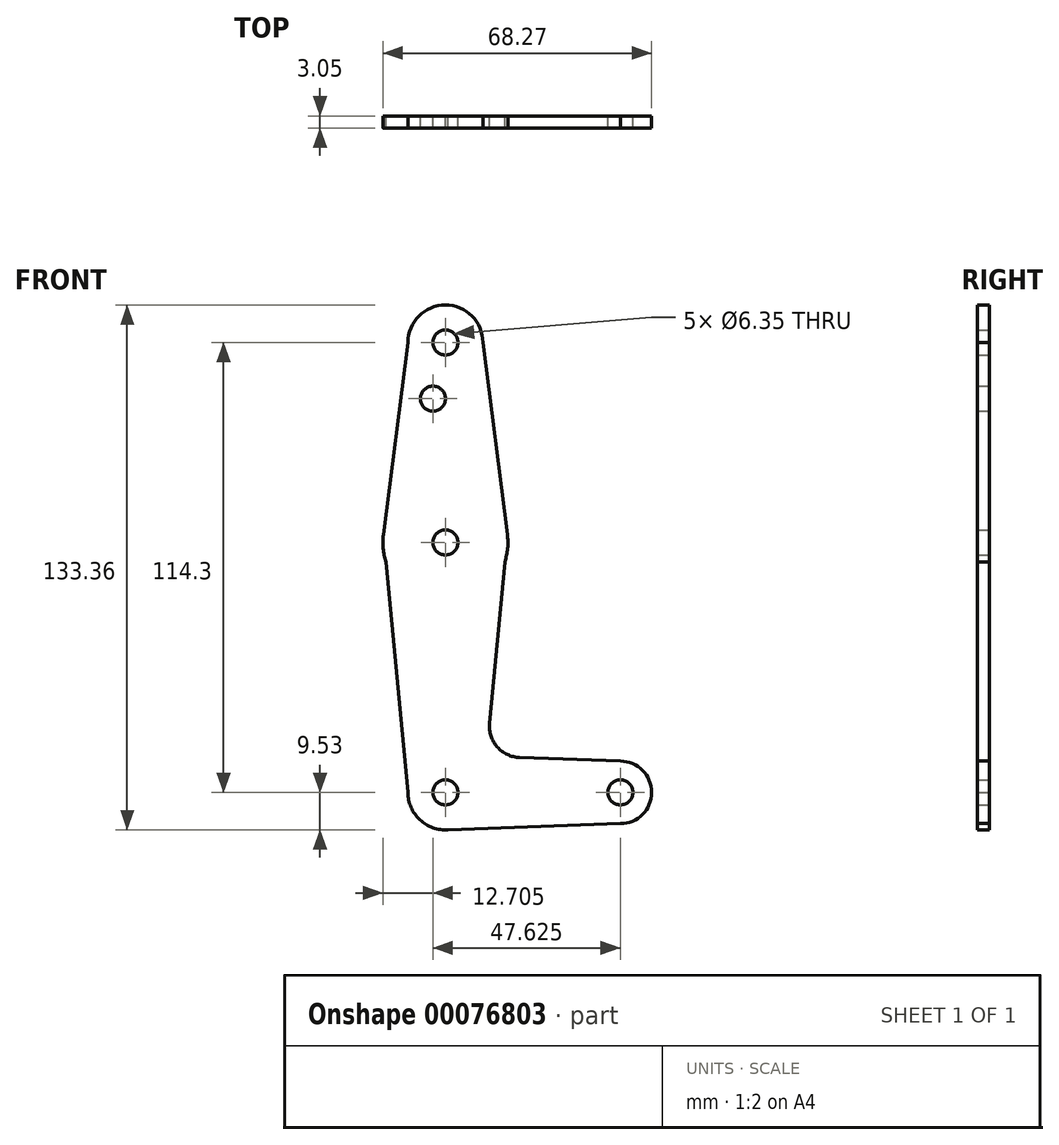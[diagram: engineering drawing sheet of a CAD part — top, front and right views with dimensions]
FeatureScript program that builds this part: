
annotation { "Feature Type Name" : "Feature", "Feature Type Description" : "" }
export const myFeature = defineFeature(function(context is Context, id is Id, definition is map)
    precondition{}
    {
        {
            var Q0;
            Q0=qCreatedBy(makeId("Front.planeOp"),FACE);
            var sketch = newSketch(context, id + "F0", { "sketchPlane" : qUnion([Q0])});
            skCircle(sketch, "E0", {"center": v(0, 114.3) * mm, "radius": 9.53 * mm});
            skLineSegment(sketch, "E1", {"start": v(0, 114.3) * mm, "end": v(0, 63.5) * mm, "construction": true});
            skCircle(sketch, "E2", {"center": v(0, 63.5) * mm, "radius": 15.88 * mm});
            skLineSegment(sketch, "E3", {"start": v(0, 63.5) * mm, "end": v(0, 0) * mm, "construction": true});
            skCircle(sketch, "E4", {"center": v(0, 0) * mm, "radius": 9.53 * mm});
            skLineSegment(sketch, "E5", {"start": v(0, 0) * mm, "end": v(44.45, 0) * mm, "construction": true});
            skCircle(sketch, "E6", {"center": v(44.45, 0) * mm, "radius": 7.94 * mm});
            skLineSegment(sketch, "E7", {"start": v(9.52, 114.3) * mm, "end": v(15.75, 65.5) * mm});
            skLineSegment(sketch, "E8", {"start": v(-9.53, 114.3) * mm, "end": v(-15.75, 65.5) * mm});
            skLineSegment(sketch, "E9", {"start": v(0, -9.53) * mm, "end": v(44.45, -7.94) * mm});
            skCircle(sketch, "E10", {"center": v(0, 114.3) * mm, "radius": 3.18 * mm});
            skCircle(sketch, "E11", {"center": v(0, 63.5) * mm, "radius": 3.18 * mm});
            skCircle(sketch, "E12", {"center": v(0, 0) * mm, "radius": 3.18 * mm});
            skCircle(sketch, "E13", {"center": v(44.45, 0) * mm, "radius": 3.18 * mm});
            skCircle(sketch, "E14", {"center": v(-3.18, 100.03) * mm, "radius": 3.18 * mm});
            skLineSegment(sketch, "E15", {"start": v(15.75, 65.5) * mm, "end": v(11.22, 17.55) * mm});
            skLineSegment(sketch, "E16", {"start": v(44.45, 7.94) * mm, "end": v(18.85, 8.86) * mm});
            skPoint(sketch, "E17.newPointA", {"position": v(9.57, 0) * mm});
            skPoint(sketch, "E17.newPointB", {"position": v(0, 9.53) * mm});
            skArc(sketch, "E17.filletArc", {"start": v(11.22, 17.55) * mm, "mid": v(13.16, 11.56) * mm, "end": v(18.85, 8.86) * mm});
            skLineSegment(sketch, "E18", {"start": v(-9.53, 0) * mm, "end": v(-15.75, 65.5) * mm});
            skSolve(sketch);
        }
        {
            var Q0;
            Q0 = qSketchRegion(id + "F0", true);
            extrude(context, id + "F1", {"entities" : qUnion([Q0]), "depth" : 3.05 * mm});
        }
    });
